# Revit family: HLS60LM
name_source: partatom
category: Lighting Fixtures
units: mm (PartAtom-declared; Revit-internal decimal feet)

## family parameters
Cut with Voids When Loaded = No
Host = Face
Light Source = Yes
Maintain Annotation Orientation = No
Part Type = Normal
Room Calculation Point = No
Round Connector Dimension = Use Diameter
Shared = No

## types (1)
- HLS60LM
    Color Filter = 16777215
    Default Elevation = 1219.20 mm
    Dimming Lamp Color Temperature Shift = <None>
    Emit from Line Length = 609.60 mm
    Keynote = LUCE SOLARE
    Lamp = LED
    Manufacturer = BEGHELLI
    Model = HLS60LM
    POLE HEIGHT = 1550.00 mm
    POLE MATERIAL = BRACKET
    Photometric Web File = HLS60LM.IES
    Tilt Angle = 90.00°
    Type Comments = El luminario Helios de la familia PLANET SUN, integra el
panel fotovoltáico, módulos LED y batería de Li-ion. Es de bajo
mantenimiento, con alta salida de lúmenes y mayor ahorro de
energía. Incluye 3 modos o escenas de iluminación. Incluye
soporte y kit para sujeción de luminario.
    Type Image = HLS60LM IMAGE.PNG
    Wattage Comments = 32

## geometry (parser evidence)
native form markers: Sweep x14
no freeform markers — native parametric forms only
